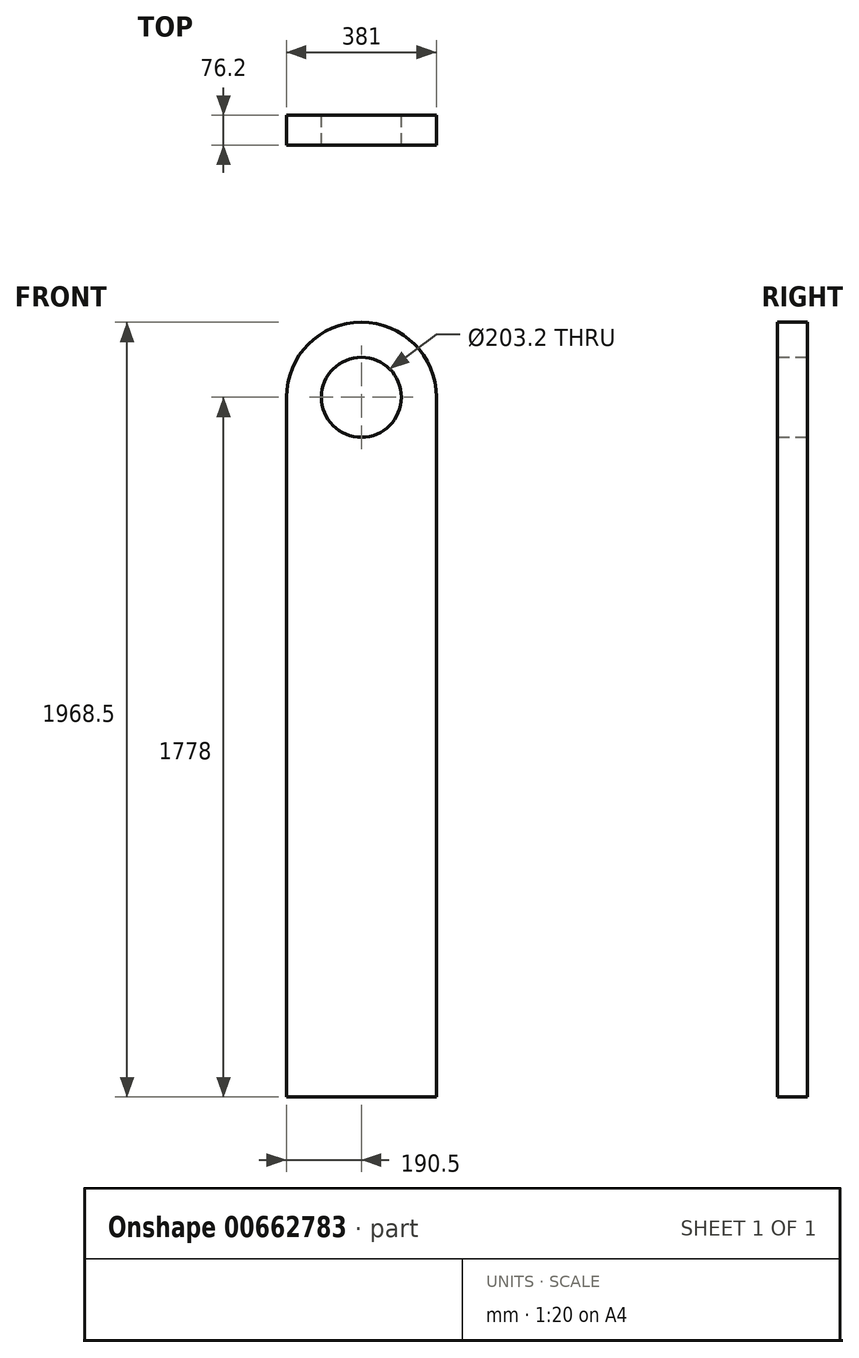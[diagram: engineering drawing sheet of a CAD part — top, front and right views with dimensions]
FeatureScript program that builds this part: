
annotation { "Feature Type Name" : "Feature", "Feature Type Description" : "" }
export const myFeature = defineFeature(function(context is Context, id is Id, definition is map)
    precondition{}
    {
        {
            var Q0;
            Q0=qCreatedBy(makeId("Front.planeOp"),FACE);
            var sketch = newSketch(context, id + "F0", { "sketchPlane" : qUnion([Q0])});
            skLineSegment(sketch, "E0.bottom", {"start": v(-190.5, 0) * mm, "end": v(190.5, 0) * mm});
            skLineSegment(sketch, "E0.left", {"start": v(-190.5, 0) * mm, "end": v(-190.5, 1778) * mm});
            skLineSegment(sketch, "E0.right", {"start": v(190.5, 0) * mm, "end": v(190.5, 1778) * mm});
            skArc(sketch, "E1", {"start": v(190.5, 1778) * mm, "mid": v(0, 1968.5) * mm, "end": v(-190.5, 1778) * mm});
            skCircle(sketch, "E2", {"center": v(0, 1778) * mm, "radius": 101.6 * mm});
            skSolve(sketch);
        }
        {
            var Q0;
            Q0 = qSketchRegion(id + "F0", true);
            extrude(context, id + "F1", {"entities" : qUnion([Q0]), "depth" : 76.2 * mm, "offsetDistance" : 25.4 * mm});
        }
    });
